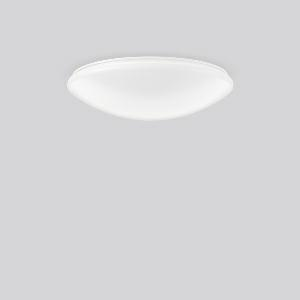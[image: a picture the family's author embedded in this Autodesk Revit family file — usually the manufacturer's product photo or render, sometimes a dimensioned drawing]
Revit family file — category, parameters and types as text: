
# Revit family: flat_polymero_312244_002_1_76_cd9b
name_source: partatom
category: Lighting Fixtures
units: mm (PartAtom-declared; Revit-internal decimal feet)

## family parameters
Cut with Voids When Loaded = No
Host = Face
Light Source = No
Part Type = Normal
Room Calculation Point = No
Round Connector Dimension = Use Diameter
Shared = No

## types (1)
- FLAT POLYMERO (1 x LED Modul 830, 3200 lm, 3000)
    Apparent Load = 32 VA
    CIE Flux Codes = 41 71 89 87 100
    Color Rendering = 80
    Color Temperature = 3000
    Default Elevation = 1800 mm
    Description = Series: FLAT POLYMERO
Decorative round surface-mounted luminaire. Base: metal, powder-coated. Diffuser made of non-yellowing plastic (PMMA), opal. Diffuser fastening: patented push system. Suitable for Ceiling mounting, Wall (surface). 
Colour: white
Diameter: 460 mm
Height: 120 mm
Lamp: LED exchangeable
Socket: without socket
Colour temperature: 3000K
Colour rendering index (CRI): 83
System power: 32 W
Rated luminous flux: 3200 lm
Beam angle Down: 119°
Luminous efficiency: 100 lm/W
Control gear: AC power, DALI dimmable
Protection class: I
Type of protection: IP 40
    Height = 120 mm
    Lamp = 1 x LED Modul 830
    Lamp Light Flux = 3200 lm
    Lamp count = 1
    Length = 460 mm
    Lifetime = 50000 h
    Luminous efficacy = 100 lm/W
    Manufacturer = RZB
    ModVariant = No
    Model = 312244.002.1.76
    Mounting Place = Ceiling, Wall
    Mounting Type = Surface mounted
    Number of Poles = 1
    OnlyDefault = Yes
    Power Factor = 1
    Product Name = FLAT POLYMERO
    Product group = Surface mounted ceiling and wall luminaires
    ProductGroupID = 305
    Protection Class = Protection class I
    Protection Degree = IP 40
    RLX_Detail_Level = 1
    RLX_Emergency_Light_Flux = 0 lm
    RLX_Emergency_Type = 0
    RLX_Emergency_Type_DB = No
    RlxData = <blob elided: 75573 chars, md5=e1268f26>
    Socket = socket
    Standby Power = 0 W
    System Light Flux = 3200 lm
    System Power = 32 W
    Type Comments = ALEA SPOT
    Type Image = 311518.002.1.jpg
    URL = http://relux.com
    VarID = ---
    Voltage = 230 V
    Voltage Range = 220-240 V
    Weight = 0.00 kg
    Width = 0 mm  [stored 0 ft]

note: [stored X ft] marks values corroborated as IEEE doubles in the binary element streams (Revit-internal decimal feet)

## geometry (parser evidence)
native form markers: Blend x4, Sweep x11
no freeform markers — native parametric forms only
